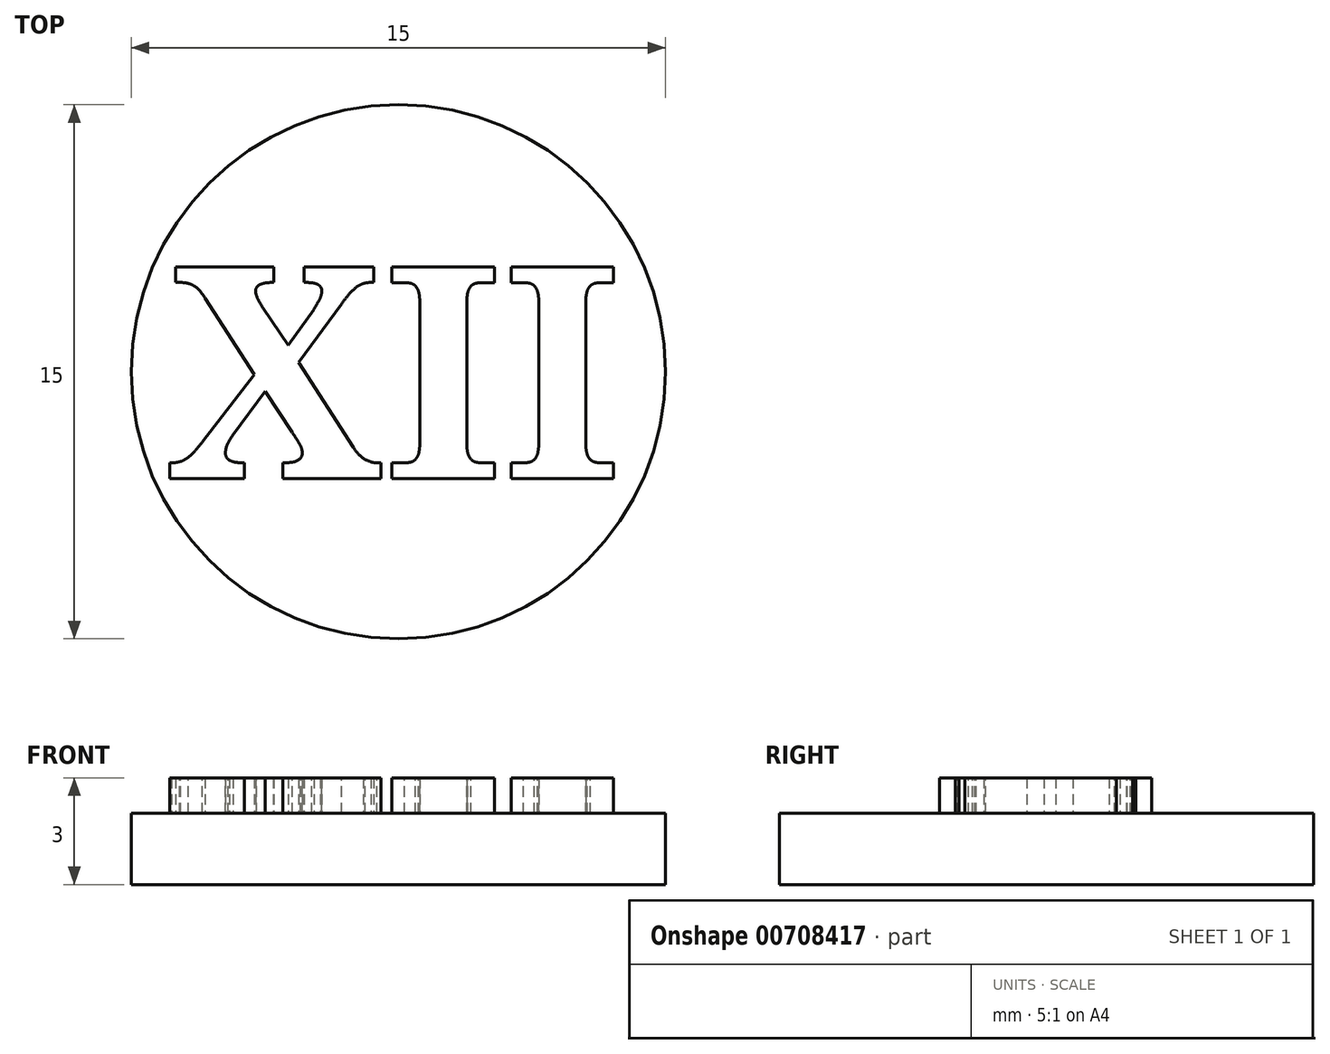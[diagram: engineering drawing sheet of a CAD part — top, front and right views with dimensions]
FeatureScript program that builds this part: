
annotation { "Feature Type Name" : "Feature", "Feature Type Description" : "" }
export const myFeature = defineFeature(function(context is Context, id is Id, definition is map)
    precondition{}
    {
        {
            var Q0;
            Q0=qCreatedBy(makeId("Top.planeOp"),FACE);
            var sketch = newSketch(context, id + "F0", { "sketchPlane" : qUnion([Q0])});
            skCircle(sketch, "E0", {"center": v(0, 0) * mm, "radius": 7.5 * mm});
            skSolve(sketch);
        }
        {
            var Q0;
            Q0=makeQuery(id+"F0.imprint","IMPRINT",FACE,{"disambiguationData":[TD([[makeQuery(id+"F0.imprint","IMPRINT",EDGE,{"derivedFrom":sQuery(id+"F0.wireOp",EDGE,"E0")}),1.0]])]});
            extrude(context, id + "F1", {"entities" : qUnion([Q0]), "depth" : 4 * mm, "offsetDistance" : 25 * mm});
        }
        {
            var Q0;
            Q0=makeQuery(id+"F1.opExtrude","CAP_FACE",FACE,{"disambiguationData":[OSD([sQuery(id+"F0.wireOp",EDGE,"E0")])],"isStart":false});
            extrude(context, id + "F2", {"entities" : qUnion([Q0]), "operationType" : NewBodyOperationType.REMOVE, "oppositeDirection" : true, "depth" : 2 * mm, "offsetDistance" : 25 * mm});
        }
        {
            var Q0;
            Q0=makeQuery(id+"F2.boolean.opBoolean","COPY",FACE,{"derivedFrom":makeQuery(id+"F2.opExtrude","CAP_FACE",FACE,{"disambiguationData":[OSD([sQuery(id+"F0.wireOp",EDGE,"E0")])],"isStart":false})});
            var sketch = newSketch(context, id + "F3", { "sketchPlane" : qUnion([Q0])});
            skText(sketch, "E1", { "text": "XII", "fontName": "NotoSerif-Bold.ttf"});
            const initialGuessF3  = {"E1": [-0.00651, -0.003, 1, 0, 0.006]};
            skSetInitialGuess(sketch, initialGuessF3);
            skSolve(sketch);
        }
        {
            var Q0;
            Q0=makeQuery(id+"F3.imprint","IMPRINT",FACE,{"disambiguationData":[TD([[makeQuery(id+"F3.imprint","IMPRINT",EDGE,{"derivedFrom":sQuery(id+"F3.wireOp",EDGE,"E1.sketch_text.stroke-0")}),-1.0]])]});
            var Q1;
            Q1=makeQuery(id+"F3.imprint","IMPRINT",FACE,{"disambiguationData":[TD([[makeQuery(id+"F3.imprint","IMPRINT",EDGE,{"derivedFrom":sQuery(id+"F3.wireOp",EDGE,"E1.sketch_text.stroke-63")}),-1.0]])]});
            var Q2;
            Q2=makeQuery(id+"F3.imprint","IMPRINT",FACE,{"disambiguationData":[TD([[makeQuery(id+"F3.imprint","IMPRINT",EDGE,{"derivedFrom":sQuery(id+"F3.wireOp",EDGE,"E1.sketch_text.stroke-91")}),-1.0]])]});
            extrude(context, id + "F4", {"entities" : qUnion([Q0, Q1, Q2]), "operationType" : NewBodyOperationType.ADD, "depth" : 1 * mm, "offsetDistance" : 25 * mm});
        }
    });
